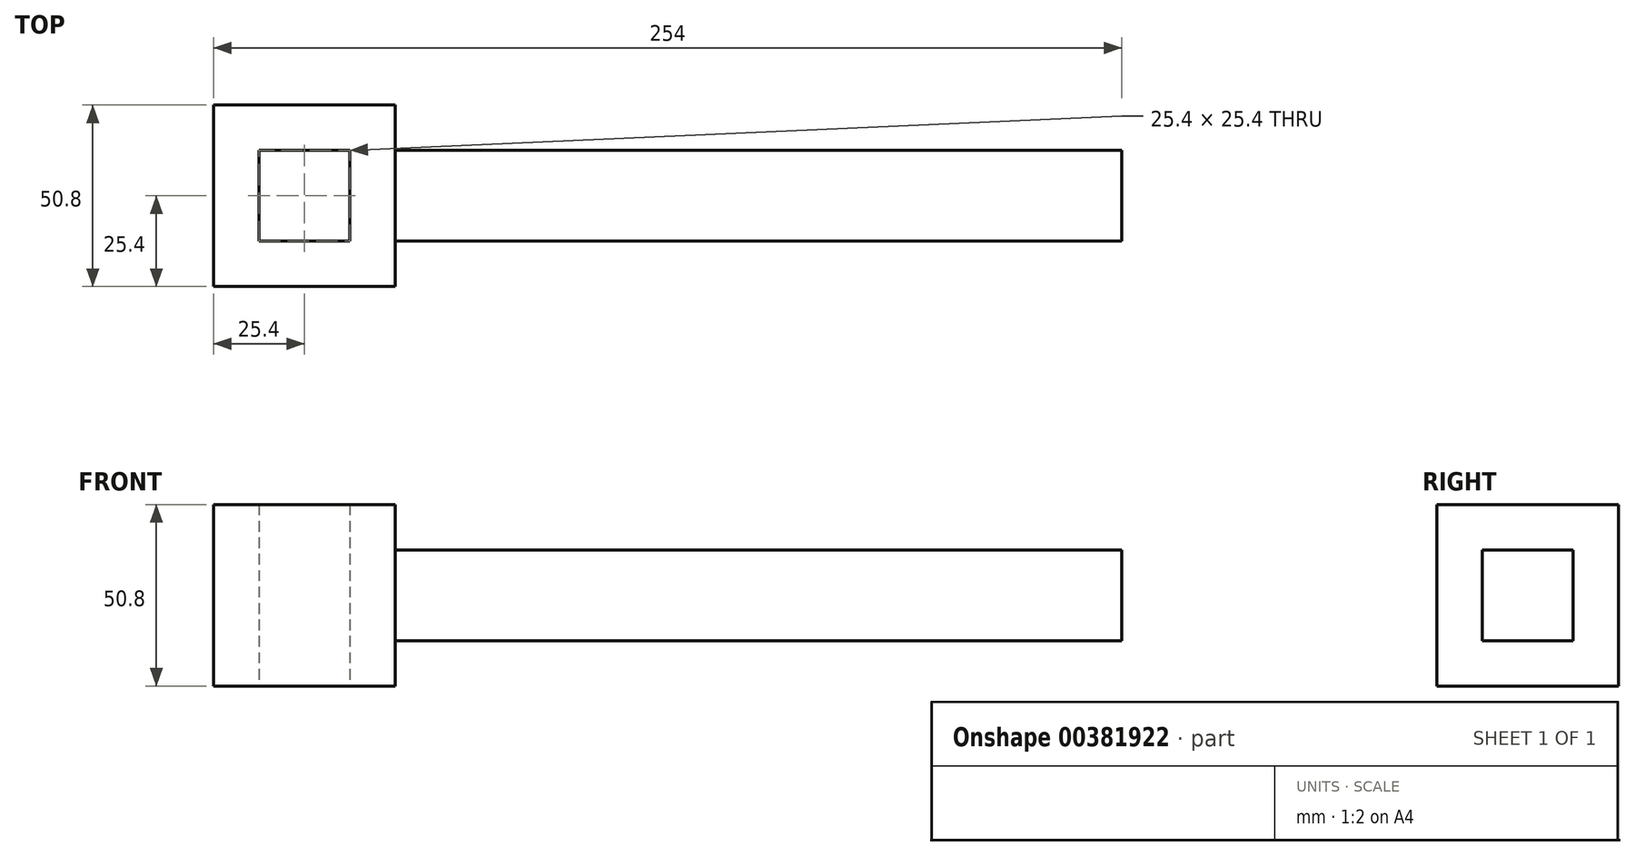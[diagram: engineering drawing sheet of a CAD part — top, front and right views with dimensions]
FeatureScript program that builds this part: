
annotation { "Feature Type Name" : "Feature", "Feature Type Description" : "" }
export const myFeature = defineFeature(function(context is Context, id is Id, definition is map)
    precondition{}
    {
        {
            var Q0;
            Q0=qCreatedBy(makeId("Top.planeOp"),FACE);
            var sketch = newSketch(context, id + "F0", { "sketchPlane" : qUnion([Q0])});
            skLineSegment(sketch, "E0.bottom", {"start": v(-25.4, 25.4) * mm, "end": v(25.4, 25.4) * mm});
            skLineSegment(sketch, "E0.top", {"start": v(-25.4, -25.4) * mm, "end": v(25.4, -25.4) * mm});
            skLineSegment(sketch, "E0.left", {"start": v(-25.4, 25.4) * mm, "end": v(-25.4, -25.4) * mm});
            skLineSegment(sketch, "E0.right", {"start": v(25.4, 25.4) * mm, "end": v(25.4, -25.4) * mm});
            skLineSegment(sketch, "E1", {"start": v(-25.4, 25.4) * mm, "end": v(25.4, -25.4) * mm, "construction": true});
            skLineSegment(sketch, "E2.bottom", {"start": v(-12.7, -12.7) * mm, "end": v(12.7, -12.7) * mm});
            skLineSegment(sketch, "E2.top", {"start": v(-12.7, 12.7) * mm, "end": v(12.7, 12.7) * mm});
            skLineSegment(sketch, "E2.left", {"start": v(-12.7, -12.7) * mm, "end": v(-12.7, 12.7) * mm});
            skLineSegment(sketch, "E2.right", {"start": v(12.7, -12.7) * mm, "end": v(12.7, 12.7) * mm});
            skLineSegment(sketch, "E3", {"start": v(-12.7, -12.7) * mm, "end": v(12.7, 12.7) * mm, "construction": true});
            skSolve(sketch);
        }
        {
            var Q0;
            Q0 = qSketchRegion(id + "F0", true);
            extrude(context, id + "F1", {"entities" : qUnion([Q0]), "depth" : 50.8 * mm});
        }
        {
            var Q0;
            Q0=makeQuery(id+"F1.opExtrude","SWEPT_FACE",FACE,{"disambiguationData":[OSD([sQuery(id+"F0.wireOp",EDGE,"E0.right")])]});
            var sketch = newSketch(context, id + "F2", { "sketchPlane" : qUnion([Q0])});
            skLineSegment(sketch, "E4.bottom", {"start": v(-12.7, 38.1) * mm, "end": v(12.7, 38.1) * mm});
            skLineSegment(sketch, "E4.top", {"start": v(-12.7, 12.7) * mm, "end": v(12.7, 12.7) * mm});
            skLineSegment(sketch, "E4.left", {"start": v(-12.7, 38.1) * mm, "end": v(-12.7, 12.7) * mm});
            skLineSegment(sketch, "E4.right", {"start": v(12.7, 38.1) * mm, "end": v(12.7, 12.7) * mm});
            skLineSegment(sketch, "E5", {"start": v(0, 0) * mm, "end": v(0, 25.4) * mm, "construction": true});
            skLineSegment(sketch, "E6", {"start": v(-12.7, 12.7) * mm, "end": v(12.7, 38.1) * mm, "construction": true});
            skSolve(sketch);
        }
        {
            var Q0;
            Q0 = qSketchRegion(id + "F2", true);
            extrude(context, id + "F3", {"entities" : qUnion([Q0]), "operationType" : NewBodyOperationType.ADD, "depth" : 203.2 * mm});
        }
    });
